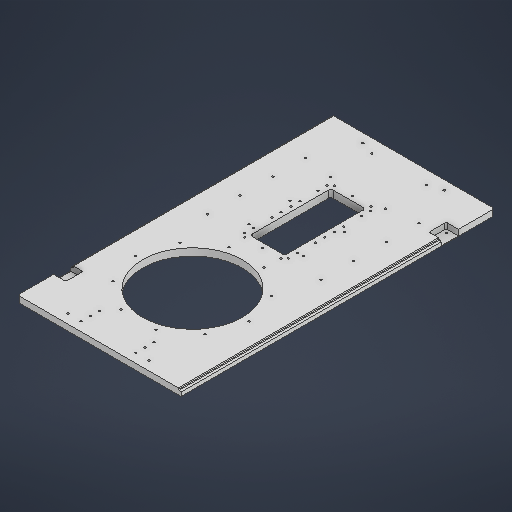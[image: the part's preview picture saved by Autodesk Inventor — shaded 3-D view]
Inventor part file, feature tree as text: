
AUTODESK INVENTOR PART (.ipt)
format: ipt  version: 2025 (Build 290162000, 162)  size: 467,968 bytes
history: native  units: in
note: dims shown in document units (in); Inventor stores cm internally (conversion verified against a paired STEP export)
features: sketch x16, extrude x5, hole x5, chamfer x5, plane x2, fillet x2
ambient origin geometry x8: Origin, YZ Plane, XZ Plane, XY Plane, X Axis, Y Axis, Z Axis, Center Point
bodies: Solid1 (feature_tree)
feature tree (35):
  extrude  "Extrusion1"  Depth=27.1654in
  sketch  "Sketch2"  dims[d5=8.6614in d6=0.0in d7=0.0in]
  extrude  "Extrusion2"  Depth=0.625in
  plane  "Work Plane1"
  hole  "Hole3"  [1 undecoded]
  sketch  "Sketch7"  dims[d69=0.1575in d70=3.937in d72=360.0deg]
  plane  "Work Plane2"
  hole  "Hole4"  [1 undecoded]
  sketch  "Sketch9"  dims[d82=1.063in]
  fillet  "Fillet2"  Radius=7.0625in
  chamfer  "Chamfer1"  Distance=3.937in Angle=360.0deg
  chamfer  "Chamfer2"  Distance=3.1102in
  extrude  "Extrusion7"  Depth=0.1969in
  extrude  "Extrusion8"  Depth=0.3937in TaperAngle=45.0deg
  chamfer  "Chamfer3"  Distance=0.0984in Angle=45.0deg
  chamfer  "Chamfer4"  Distance=0.1181in
  hole  "Hole5"  [1 undecoded]
  chamfer  "Chamfer5"  Distance=0.4951in
  hole  "Hole6"  [1 undecoded]
  sketch  "Sketch15"  dims[d86=3.1102in d87=3.1102in d88=0.1969in d89=0.0984in d90=0.0787in d91=45.0deg d92=0.0984in d93=0.0787in d94=45.0deg d95=0.1181in d96=0.1181in d97=0.4951in d98=0.0in d99=0.2362in d100=0.2362in d101=0.122in d102=0.0in d103=0.0787in d104=0.1378in d105=45.0deg d106=0.1378in d107=0.0787in d108=45.0deg d109=0.748in d110=0.315in d111=0.8661in d112=0.748in d113=0.1299in d114=0.1299in d115=0.1299in d116=0.1299in d118=0.315in d119=0.8661in d120=0.748in d121=0.748in d122=0.1276in d123=0.315in d124=0.1575in d125=0.0787in d126=90.0deg d127=0.315in d128=0.8108in d129=0.0138in d130=0.0787in d131=45.0deg d146=3.9469in d147=0.7874in d148=0.3937in d149=0.1575in d150=3.937in d152=1.1811in d153=0.3937in d155=0.3937in d157=0.1575in d158=1.1811in d160=0.7874in d161=0.3937in d163=0.3937in d165=9.8425in d166=0.1575in d167=2.9528in d168=1.1811in d169=3.1496in d171=1.4173in d172=0.3937in d174=0.3937in d176=0.1628in d177=0.3937in d178=0.1575in d179=0.0787in d180=90.0deg d181=0.3937in d182=0.8108in d191=3.0in d192=7.0in d193=6.4961in d194=0.8312in d195=0.0in d196=0.1969in d197=0.3937in d198=0.1969in d199=1.9685in d201=0.7874in d202=0.3937in d204=0.3937in d206=0.3189in d207=0.1969in d208=0.3189in d209=1.9685in d211=0.7874in d212=0.3937in d214=0.3937in d216=0.1628in d217=0.3937in d218=0.1575in d219=0.0787in d220=90.0deg d221=0.3937in d222=0.8108in d26=0.0394in d27=0.0394in d28=0.0394in d29=0.0059in d30=0.0098in d31=0.0148in d32=0.5635in d33=0.0295in d34=0.8108in d35=0.0025in d36=0.0295in d37=0.0148in d66=0.0197in d67=0.0344in]
  extrude  "Extrusion11"  Depth=0.2362in
  fillet  "Fillet3"  Radius=0.122in
  hole  "Hole7"  [1 undecoded]
  sketch  "Sketch1"  dims[d0=14.1732in d1=27.1654in]
  sketch  "Sketch6"  dims[d68=9.8425in]
  sketch  "Sketch8"  dims[d74=0.1628in d75=0.3937in d76=0.1575in d77=0.0787in d78=90.0deg d79=0.3937in d80=0.8108in]
  sketch  "Sketch Circular Pattern4"  dims[d57=0.1936in d58=0.1969in d59=0.1575in d60=0.0787in d61=90.0deg d62=0.1969in d63=0.8108in]
  sketch  "Sketch10"  dims[d83=1.063in]
  sketch  "Sketch11"  dims[d84=1.4961in]
  sketch  "Sketch12"  dims[d85=1.4961in]
  sketch  "Sketch Rectangular Pattern1"  dims[d2=0.625in d3=0.0in d4=8.0709in]
  sketch  "Sketch Rectangular Pattern2"  dims[d8=10.6299in d50=5.9055in d55=7.0625in]
  sketch  "Sketch Rectangular Pattern3"  dims[d56=25.5906in]
  sketch  "Sketch Rectangular Pattern4"  dims[d64=10.3543in]
  sketch  "Sketch Rectangular Pattern5"  dims[d65=10.6299in]
note: 5 required parameter values undecoded (feature->parameter linkage not recoverable at this tier; creation-order binding heuristic only, values carry confidence <= 0.55)
